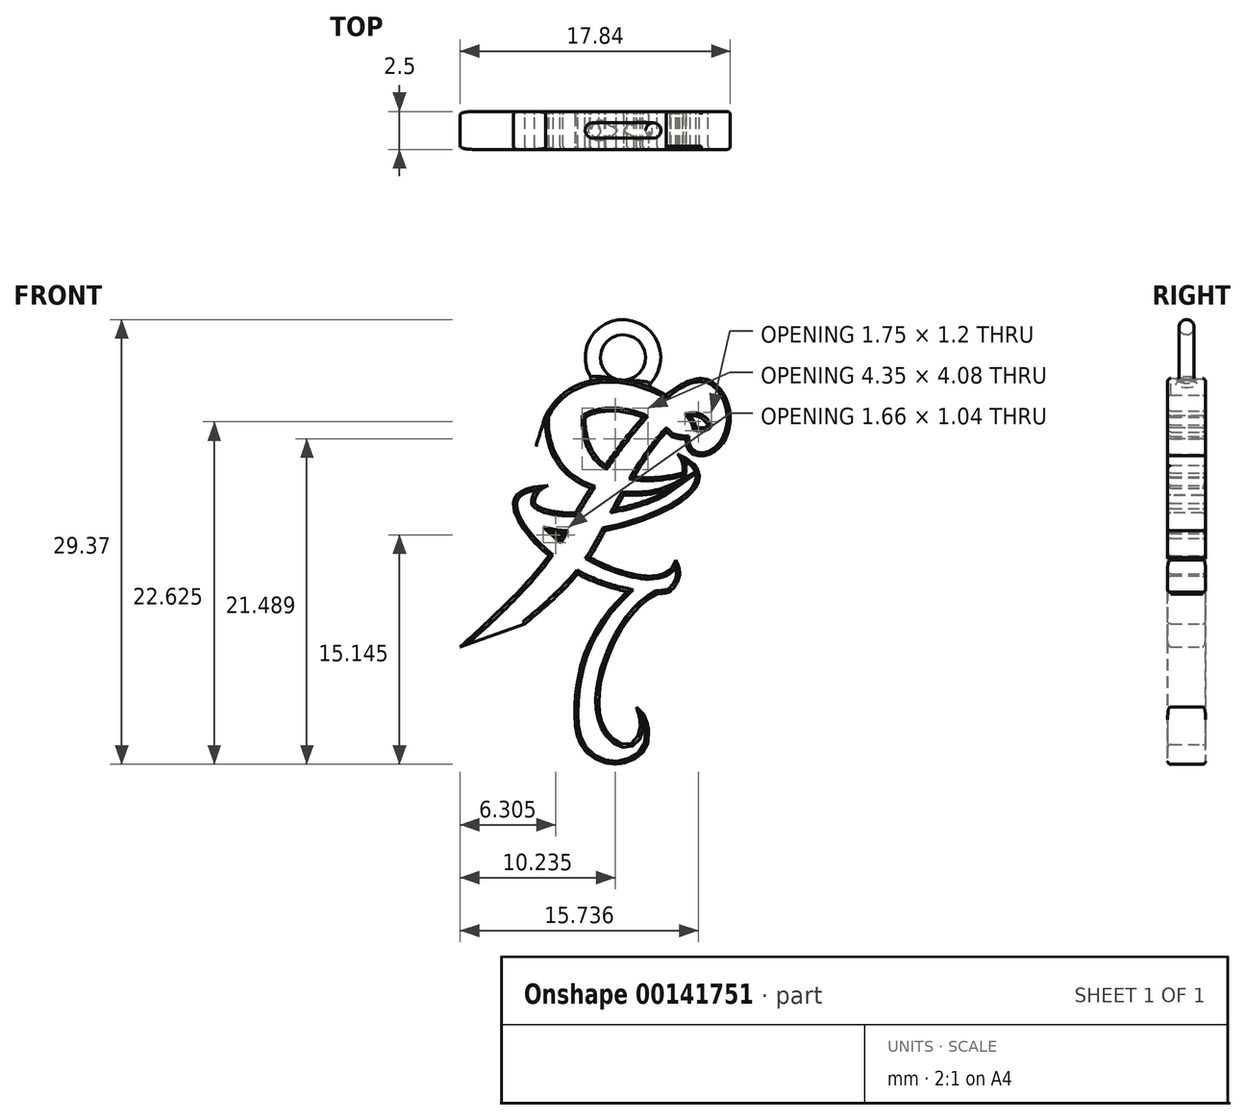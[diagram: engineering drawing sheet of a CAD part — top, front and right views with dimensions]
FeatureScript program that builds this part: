
annotation { "Feature Type Name" : "Feature", "Feature Type Description" : "" }
export const myFeature = defineFeature(function(context is Context, id is Id, definition is map)
    precondition{}
    {
        {
            var Q0;
            Q0=qCreatedBy(makeId("Front.planeOp"),FACE);
            var sketch = newSketch(context, id + "F0", { "sketchPlane" : qUnion([Q0])});
            skLineSegment(sketch, "E0.bottom", {"start": v(0, 0) * mm, "end": v(12.5, 0) * mm, "construction": true});
            skLineSegment(sketch, "E0.top", {"start": v(0, 25.5) * mm, "end": v(12.5, 25.5) * mm, "construction": true});
            skLineSegment(sketch, "E0.left", {"start": v(0, 0) * mm, "end": v(0, 25.5) * mm, "construction": true});
            skLineSegment(sketch, "E0.right", {"start": v(12.5, 0) * mm, "end": v(12.5, 25.5) * mm, "construction": true});
            skFitSpline(sketch, "E1", {"points": [v(0.9, 3.9) * mm, v(1.62, 1.47) * mm, v(0.92, 0.6) * mm, v(-0.5, 0.13) * mm, v(-2.58, 1.12) * mm, v(-3.17, 4.25) * mm, v(-2.44, 7.64) * mm, v(-1.46, 9.5) * mm, v(0.26, 11.54) * mm], "startDerivative": vector(17.77, -10.4) * mm, "endDerivative": vector(26.54, 27.1) * mm});
            skFitSpline(sketch, "E2", {"points": [v(-4.96, 18.54) * mm, v(-7.22, 17.42) * mm, v(-4.26, 13.45) * mm, v(3.06, 11.5) * mm], "startDerivative": vector(-17.4, -1.02) * mm, "endDerivative": vector(13.96, 3.31) * mm});
            skFitSpline(sketch, "E3", {"points": [v(3.06, 11.5) * mm, v(3.48, 13.61) * mm], "startDerivative": vector(2.83, 2.53) * mm, "endDerivative": vector(-0.9, 1.59) * mm});
            skFitSpline(sketch, "E4", {"points": [v(3.48, 13.61) * mm, v(-4.96, 18.54) * mm], "startDerivative": vector(-2.82, -10.87) * mm, "endDerivative": vector(12.42, 5.48) * mm});
            skCircle(sketch, "E5", {"center": v(1.14, 27.32) * mm, "radius": 0.4 * mm, "construction": true});
            skFitSpline(sketch, "E6", {"points": [v(0.9, 3.9) * mm, v(1.13, 3) * mm, v(1.03, 2.09) * mm, v(0.45, 1.46) * mm, v(-0.56, 1.7) * mm, v(-1.47, 3.16) * mm, v(-1.45, 5.64) * mm, v(-0.38, 8.55) * mm, v(1.1, 10.57) * mm, v(2.25, 11.38) * mm], "startDerivative": vector(3.49, -10.6) * mm, "endDerivative": vector(12.87, 6.76) * mm});
            skFitSpline(sketch, "E7", {"points": [v(-5.84, 17.36) * mm, v(3.62, 20.6) * mm], "startDerivative": vector(4.26, -4.9) * mm, "endDerivative": vector(-7.23, 9.47) * mm});
            skFitSpline(sketch, "E8", {"points": [v(-4.62, 15.45) * mm, v(3.62, 20.6) * mm], "startDerivative": vector(11.81, -2.43) * mm, "endDerivative": vector(-14.87, 6.6) * mm});
            skFitSpline(sketch, "E9", {"points": [v(3.15, 18.37) * mm, v(-5.12, 23.16) * mm], "startDerivative": vector(-5.6, -2.83) * mm, "endDerivative": vector(0.7, 17.4) * mm});
            skFitSpline(sketch, "E10", {"points": [v(3.94, 19.38) * mm, v(-2.5, 23.06) * mm], "startDerivative": vector(-9.58, -2.63) * mm, "endDerivative": vector(0.35, 11.22) * mm});
            skFitSpline(sketch, "E11", {"points": [v(-5.12, 23.16) * mm, v(4.83, 22.38) * mm], "startDerivative": vector(7.14, 13.52) * mm, "endDerivative": vector(2.17, -7.79) * mm});
            skFitSpline(sketch, "E12", {"points": [v(-2.5, 23.06) * mm, v(3.17, 21.8) * mm], "startDerivative": vector(5.66, 2.86) * mm, "endDerivative": vector(3.86, -4.07) * mm});
            skFitSpline(sketch, "E13", {"points": [v(3.17, 21.8) * mm, v(4.15, 21.6) * mm], "startDerivative": vector(0.91, -0.36) * mm, "endDerivative": vector(1.08, 0) * mm});
            skFitSpline(sketch, "E14", {"points": [v(4.83, 22.38) * mm, v(5.62, 22.54) * mm], "startDerivative": vector(0.9, -0.04) * mm, "endDerivative": vector(0.4, 0.77) * mm});
            skFitSpline(sketch, "E15", {"points": [v(4.15, 21.6) * mm, v(5.91, 20.7) * mm, v(7.03, 23.56) * mm, v(5.18, 25.62) * mm], "startDerivative": vector(-0.4, -12.26) * mm, "endDerivative": vector(-7.72, 0.04) * mm});
            skFitSpline(sketch, "E16", {"points": [v(5.62, 22.54) * mm, v(-0.36, 17.18) * mm, v(-6.48, 9.4) * mm], "startDerivative": vector(-9.74, 14.63) * mm, "endDerivative": vector(-24.26, -19.86) * mm});
            skFitSpline(sketch, "E17", {"points": [v(5.18, 25.62) * mm, v(-2.88, 17.18) * mm, v(-10.76, 7.88) * mm], "startDerivative": vector(-15.54, -0.02) * mm, "endDerivative": vector(-34.83, -31.36) * mm});
            skFitSpline(sketch, "E18", {"points": [v(-10.76, 7.88) * mm, v(-6.48, 9.4) * mm], "startDerivative": vector(4.28, 1.52) * mm, "endDerivative": vector(4.28, 1.52) * mm});
            skSolve(sketch);
        }
        {
            var Q0;
            {var subQ0=sQuery(id+"F0.wireOp",EDGE,"E3");Q0=makeQuery(id+"F0.imprint","IMPRINT",FACE,{"disambiguationData":[TD([[makeQuery(id+"F0.imprint","IMPRINT",EDGE,{"derivedFrom":subQ0}),1.0]])]});}
            var Q1;
            {var subQ0=sQuery(id+"F0.wireOp",EDGE,"E1");Q1=makeQuery(id+"F0.imprint","IMPRINT",FACE,{"disambiguationData":[TD([[makeQuery(id+"F0.imprint","IMPRINT",EDGE,{"derivedFrom":subQ0}),-1.0]])]});}
            var Q2;
            {var subQ5=sQuery(id+"F0.wireOp",EDGE,"E18");Q2=makeQuery(id+"F0.imprint","IMPRINT",FACE,{"disambiguationData":[TD([[makeQuery(id+"F0.imprint","IMPRINT",EDGE,{"derivedFrom":subQ5}),1.0]])]});}
            var Q3;
            {var subQ0=sQuery(id+"F0.wireOp",EDGE,"E17");var subQ1=sQuery(id+"F0.wireOp",EDGE,"E2");var subQ2=makeQuery(id+"F0.imprint","INTERSECT",VERTEX,{"derivedFrom":[subQ1,subQ0]});Q3=makeQuery(id+"F0.imprint","IMPRINT",FACE,{"disambiguationData":[TD([[makeQuery(id+"F0.imprint","IMPRINT",EDGE,{"disambiguationData":[TD([[subQ2,-1.0]])],"derivedFrom":subQ1}),1.0]])]});}
            var Q4;
            {var subQ0=sQuery(id+"F0.wireOp",EDGE,"E4");var subQ5=sQuery(id+"F0.wireOp",EDGE,"E2");var subQ6=makeQuery(id+"F0.imprint","INTERSECT",VERTEX,{"derivedFrom":[subQ5,subQ0]});Q4=makeQuery(id+"F0.imprint","IMPRINT",FACE,{"disambiguationData":[TD([[makeQuery(id+"F0.imprint","IMPRINT",EDGE,{"disambiguationData":[TD([[subQ6,-1.0]])],"derivedFrom":subQ5}),1.0]])]});}
            var Q5;
            {var subQ0=sQuery(id+"F0.wireOp",EDGE,"E7");var subQ1=sQuery(id+"F0.wireOp",EDGE,"E4");var subQ2=makeQuery(id+"F0.imprint","INTERSECT",VERTEX,{"derivedFrom":[subQ1,subQ0]});Q5=makeQuery(id+"F0.imprint","IMPRINT",FACE,{"disambiguationData":[TD([[makeQuery(id+"F0.imprint","IMPRINT",EDGE,{"disambiguationData":[TD([[subQ2,1.0]])],"derivedFrom":subQ1}),-1.0]])]});}
            var Q6;
            {var subQ0=sQuery(id+"F0.wireOp",EDGE,"E16");var subQ1=sQuery(id+"F0.wireOp",EDGE,"E4");var subQ2=makeQuery(id+"F0.imprint","INTERSECT",VERTEX,{"derivedFrom":[subQ1,subQ0]});Q6=makeQuery(id+"F0.imprint","IMPRINT",FACE,{"disambiguationData":[TD([[makeQuery(id+"F0.imprint","IMPRINT",EDGE,{"disambiguationData":[TD([[subQ2,-1.0]])],"derivedFrom":subQ1}),-1.0]])]});}
            var Q7;
            {var subQ0=sQuery(id+"F0.wireOp",EDGE,"E17");var subQ1=sQuery(id+"F0.wireOp",EDGE,"E7");var subQ2=makeQuery(id+"F0.imprint","INTERSECT",VERTEX,{"derivedFrom":[subQ1,subQ0]});Q7=makeQuery(id+"F0.imprint","IMPRINT",FACE,{"disambiguationData":[TD([[makeQuery(id+"F0.imprint","IMPRINT",EDGE,{"disambiguationData":[TD([[subQ2,-1.0]])],"derivedFrom":subQ1}),-1.0]])]});}
            var Q8;
            {var subQ1=sQuery(id+"F0.wireOp",EDGE,"E7");var subQ4=makeQuery(id+"F0.imprint","INTERSECT",VERTEX,{"derivedFrom":[subQ1,sQuery(id+"F0.wireOp",EDGE,"E9")]});Q8=makeQuery(id+"F0.imprint","IMPRINT",FACE,{"disambiguationData":[TD([[makeQuery(id+"F0.imprint","IMPRINT",EDGE,{"disambiguationData":[TD([[subQ4,1.0]])],"derivedFrom":subQ1}),-1.0]])]});}
            var Q9;
            {var subQ0=sQuery(id+"F0.wireOp",EDGE,"E9");var subQ1=sQuery(id+"F0.wireOp",EDGE,"E7");var subQ2=makeQuery(id+"F0.imprint","INTERSECT",VERTEX,{"derivedFrom":[subQ1,subQ0]});Q9=makeQuery(id+"F0.imprint","IMPRINT",FACE,{"disambiguationData":[TD([[makeQuery(id+"F0.imprint","IMPRINT",EDGE,{"disambiguationData":[TD([[subQ2,-1.0]])],"derivedFrom":subQ1}),1.0]])]});}
            var Q10;
            {var subQ0=sQuery(id+"F0.wireOp",EDGE,"E17");var subQ1=sQuery(id+"F0.wireOp",EDGE,"E7");var subQ2=makeQuery(id+"F0.imprint","INTERSECT",VERTEX,{"derivedFrom":[subQ1,subQ0]});Q10=makeQuery(id+"F0.imprint","IMPRINT",FACE,{"disambiguationData":[TD([[makeQuery(id+"F0.imprint","IMPRINT",EDGE,{"disambiguationData":[TD([[subQ2,-1.0]])],"derivedFrom":subQ1}),1.0]])]});}
            var Q11;
            {var subQ0=sQuery(id+"F0.wireOp",EDGE,"E17");var subQ1=sQuery(id+"F0.wireOp",EDGE,"E9");var subQ2=makeQuery(id+"F0.imprint","INTERSECT",VERTEX,{"derivedFrom":[subQ1,subQ0]});Q11=makeQuery(id+"F0.imprint","IMPRINT",FACE,{"disambiguationData":[TD([[makeQuery(id+"F0.imprint","IMPRINT",EDGE,{"disambiguationData":[TD([[subQ2,1.0]])],"derivedFrom":subQ1}),-1.0]])]});}
            var Q12;
            {var subQ5=sQuery(id+"F0.wireOp",EDGE,"E11");var subQ6=sQuery(id+"F0.wireOp",EDGE,"E9");var subQ7=makeQuery(id+"F0.imprint","INTERSECT",VERTEX,{"derivedFrom":[subQ6,subQ5]});Q12=makeQuery(id+"F0.imprint","IMPRINT",FACE,{"disambiguationData":[TD([[makeQuery(id+"F0.imprint","IMPRINT",EDGE,{"disambiguationData":[TD([[subQ7,1.0]])],"derivedFrom":subQ6}),-1.0]])]});}
            var Q13;
            {var subQ0=sQuery(id+"F0.wireOp",EDGE,"E16");var subQ1=sQuery(id+"F0.wireOp",EDGE,"E10");var subQ2=makeQuery(id+"F0.imprint","INTERSECT",VERTEX,{"derivedFrom":[subQ1,subQ0]});Q13=makeQuery(id+"F0.imprint","IMPRINT",FACE,{"disambiguationData":[TD([[makeQuery(id+"F0.imprint","IMPRINT",EDGE,{"disambiguationData":[TD([[subQ2,-1.0]])],"derivedFrom":subQ1}),-1.0]])]});}
            var Q14;
            {var subQ0=sQuery(id+"F0.wireOp",EDGE,"E17");var subQ1=sQuery(id+"F0.wireOp",EDGE,"E11");var subQ2=makeQuery(id+"F0.imprint","INTERSECT",VERTEX,{"derivedFrom":[subQ1,subQ0]});Q14=makeQuery(id+"F0.imprint","IMPRINT",FACE,{"disambiguationData":[TD([[makeQuery(id+"F0.imprint","IMPRINT",EDGE,{"disambiguationData":[TD([[subQ2,-1.0]])],"derivedFrom":subQ1}),-1.0]])]});}
            var Q15;
            {var subQ0=sQuery(id+"F0.wireOp",EDGE,"E13");Q15=makeQuery(id+"F0.imprint","IMPRINT",FACE,{"disambiguationData":[TD([[makeQuery(id+"F0.imprint","IMPRINT",EDGE,{"derivedFrom":subQ0}),1.0]])]});}
            extrude(context, id + "F1", {"entities" : qUnion([Q0, Q1, Q2, Q3, Q4, Q5, Q6, Q7, Q8, Q9, Q10, Q11, Q12, Q13, Q14, Q15]), "depth" : 1.25 * mm, "offsetDistance" : 25 * mm, "hasSecondDirection" : true, "secondDirectionOppositeDirection" : true, "secondDirectionDepth" : 1.25 * mm});
        }
        {
            var Q0;
            Q0=makeQuery(id+"F1.opExtrude","CAP_EDGE",EDGE,{"disambiguationData":[OSD([sQuery(id+"F0.wireOp",EDGE,"4681fdc7-3070-4394-86cc-40bf6d9edfaf")])],"isStart":false});
            var Q1;
            Q1=makeQuery(id+"F1.opExtrude","CAP_FACE",FACE,{"disambiguationData":[OSD([sQuery(id+"F0.wireOp",EDGE,"4681fdc7-3070-4394-86cc-40bf6d9edfaf"),sQuery(id+"F0.wireOp",EDGE,"8c27ad56-a9f0-494b-b41c-2942c247f4c6"),sQuery(id+"F0.wireOp",EDGE,"f5e0758e-03f0-4c22-9960-8cbbef7d2f47"),sQuery(id+"F0.wireOp",EDGE,"3a872d37-1245-47a6-877a-3f2e58ba2b5f"),sQuery(id+"F0.wireOp",EDGE,"DYU3Zu34-DmmR-dnbN-u9n5-0PIQUu0Xy99a"),sQuery(id+"F0.wireOp",EDGE,"28485420-370c-429b-b7ea-971533ee887e"),sQuery(id+"F0.wireOp",EDGE,"E1"),sQuery(id+"F0.wireOp",EDGE,"b2d6f1f3-02ad-49aa-b6fe-aaa647de590c"),sQuery(id+"F0.wireOp",EDGE,"E2"),sQuery(id+"F0.wireOp",EDGE,"E3"),sQuery(id+"F0.wireOp",EDGE,"5b510dd0-313c-4d0d-92ab-dbbb8d0ca943"),sQuery(id+"F0.wireOp",EDGE,"E4")])],"isStart":false});
            var Q2;
            Q2=makeQuery(id+"F1.opExtrude","CAP_FACE",FACE,{"disambiguationData":[OSD([sQuery(id+"F0.wireOp",EDGE,"4681fdc7-3070-4394-86cc-40bf6d9edfaf"),sQuery(id+"F0.wireOp",EDGE,"8c27ad56-a9f0-494b-b41c-2942c247f4c6"),sQuery(id+"F0.wireOp",EDGE,"f5e0758e-03f0-4c22-9960-8cbbef7d2f47"),sQuery(id+"F0.wireOp",EDGE,"3a872d37-1245-47a6-877a-3f2e58ba2b5f"),sQuery(id+"F0.wireOp",EDGE,"DYU3Zu34-DmmR-dnbN-u9n5-0PIQUu0Xy99a"),sQuery(id+"F0.wireOp",EDGE,"28485420-370c-429b-b7ea-971533ee887e"),sQuery(id+"F0.wireOp",EDGE,"E1"),sQuery(id+"F0.wireOp",EDGE,"b2d6f1f3-02ad-49aa-b6fe-aaa647de590c"),sQuery(id+"F0.wireOp",EDGE,"E2"),sQuery(id+"F0.wireOp",EDGE,"E3"),sQuery(id+"F0.wireOp",EDGE,"5b510dd0-313c-4d0d-92ab-dbbb8d0ca943"),sQuery(id+"F0.wireOp",EDGE,"E4")])],"isStart":true});
            fillet(context, id + "F2", {"entities" : qUnion([Q0, Q1, Q2]), "tangentPropagation" : true, "radius" : 0.2 * mm, "defaultsChanged" : false, "vertexSettings" : [], "allowEdgeOverflow" : false});
        }
        {
            var Q0;
            Q0=qCreatedBy(makeId("Right.planeOp"),FACE);
            var sketch = newSketch(context, id + "F3", { "sketchPlane" : qUnion([Q0])});
            skCircle(sketch, "E19", {"center": v(0, 25) * mm, "radius": 0.5 * mm});
            skLineSegment(sketch, "E20", {"start": v(-3.3, 27) * mm, "end": v(3.34, 27) * mm, "construction": true});
            skSolve(sketch);
        }
        {
            var Q0;
            Q0=qSketchRegion(id+"F3",true);
            var Q1;
            Q1=sQuery(id+"F3.wireOp",EDGE,"E20");
            revolve(context, id + "F4", {"operationType" : NewBodyOperationType.ADD, "surfaceOperationType" : NewSurfaceOperationType.NEW, "entities" : qUnion([Q0]), "axis" : qUnion([Q1]), "revolveType" : RevolveType.FULL});
        }
        {
            var Q0;
            {var subQ0=sQuery(id+"F0.wireOp",EDGE,"E11");Q0=makeQuery(id+"F4.boolean.opBoolean","INTERSECT",EDGE,{"disambiguationData":[OD(0.0)],"derivedFrom":[makeQuery(id+"F1.opExtrude","SWEPT_FACE",FACE,{"disambiguationData":[OSD([subQ0]),TDD([makeQuery(id+"F0.imprint","IMPRINT",EDGE,{"disambiguationData":[TD([[makeQuery(id+"F0.imprint","INTERSECT",VERTEX,{"derivedFrom":[sQuery(id+"F0.wireOp",EDGE,"E9"),subQ0]}),-1.0]])],"derivedFrom":subQ0})])]}),makeQuery(id+"F4.opRevolve","SWEPT_FACE",FACE,{"disambiguationData":[OSD([sQuery(id+"F3.wireOp",EDGE,"E19")])]})]});}
            var Q1;
            {var subQ0=sQuery(id+"F0.wireOp",EDGE,"E11");Q1=makeQuery(id+"F4.boolean.opBoolean","INTERSECT",EDGE,{"disambiguationData":[OD(1.0)],"derivedFrom":[makeQuery(id+"F1.opExtrude","SWEPT_FACE",FACE,{"disambiguationData":[OSD([subQ0]),TDD([makeQuery(id+"F0.imprint","IMPRINT",EDGE,{"disambiguationData":[TD([[makeQuery(id+"F0.imprint","INTERSECT",VERTEX,{"derivedFrom":[sQuery(id+"F0.wireOp",EDGE,"E9"),subQ0]}),-1.0]])],"derivedFrom":subQ0})])]}),makeQuery(id+"F4.opRevolve","SWEPT_FACE",FACE,{"disambiguationData":[OSD([sQuery(id+"F3.wireOp",EDGE,"E19")])]})]});}
            fillet(context, id + "F5", {"entities" : qUnion([Q0, Q1]), "tangentPropagation" : true, "radius" : 0.2 * mm, "defaultsChanged" : true, "vertexSettings" : [], "allowEdgeOverflow" : false});
        }
    });
